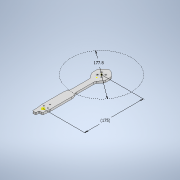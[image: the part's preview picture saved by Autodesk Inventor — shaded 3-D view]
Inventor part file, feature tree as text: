
AUTODESK INVENTOR PART (.ipt)
format: ipt  version: 2020 (Build 240168000, 168)  size: 249,856 bytes
history: native  units: in
note: dims shown in document units (in); Inventor stores cm internally (conversion verified against a paired STEP export)
features: sketch x3, extrude x2, fillet x2
ambient origin geometry x8: Origin, YZ Plane, XZ Plane, XY Plane, X Axis, Y Axis, Z Axis, Center Point
bodies: Body1 (feature_tree)
feature tree (7):
  extrude  "Extrusion1"  Depth=0.2362in
  sketch  "Sketch4"  dims[d7=0.4724in d9=7.0in d10=6.8898in d11=6.8898in]
  extrude  "Extrusion2"  Depth=7.0in
  fillet  "Fillet2"  Radius=6.8898in
  fillet  "Fillet3"  Radius=6.8898in
  sketch  "Sketch3"  dims[d2=0.2362in d3=0.0in d4=0.8352in]
  sketch  "Sketch5"  dims[d12=0.2953in d13=0.2953in d14=0.9835in d15=0.9835in d16=0.9835in d17=0.1181in d18=0.0in d20=0.3937in d21=0.7874in]
